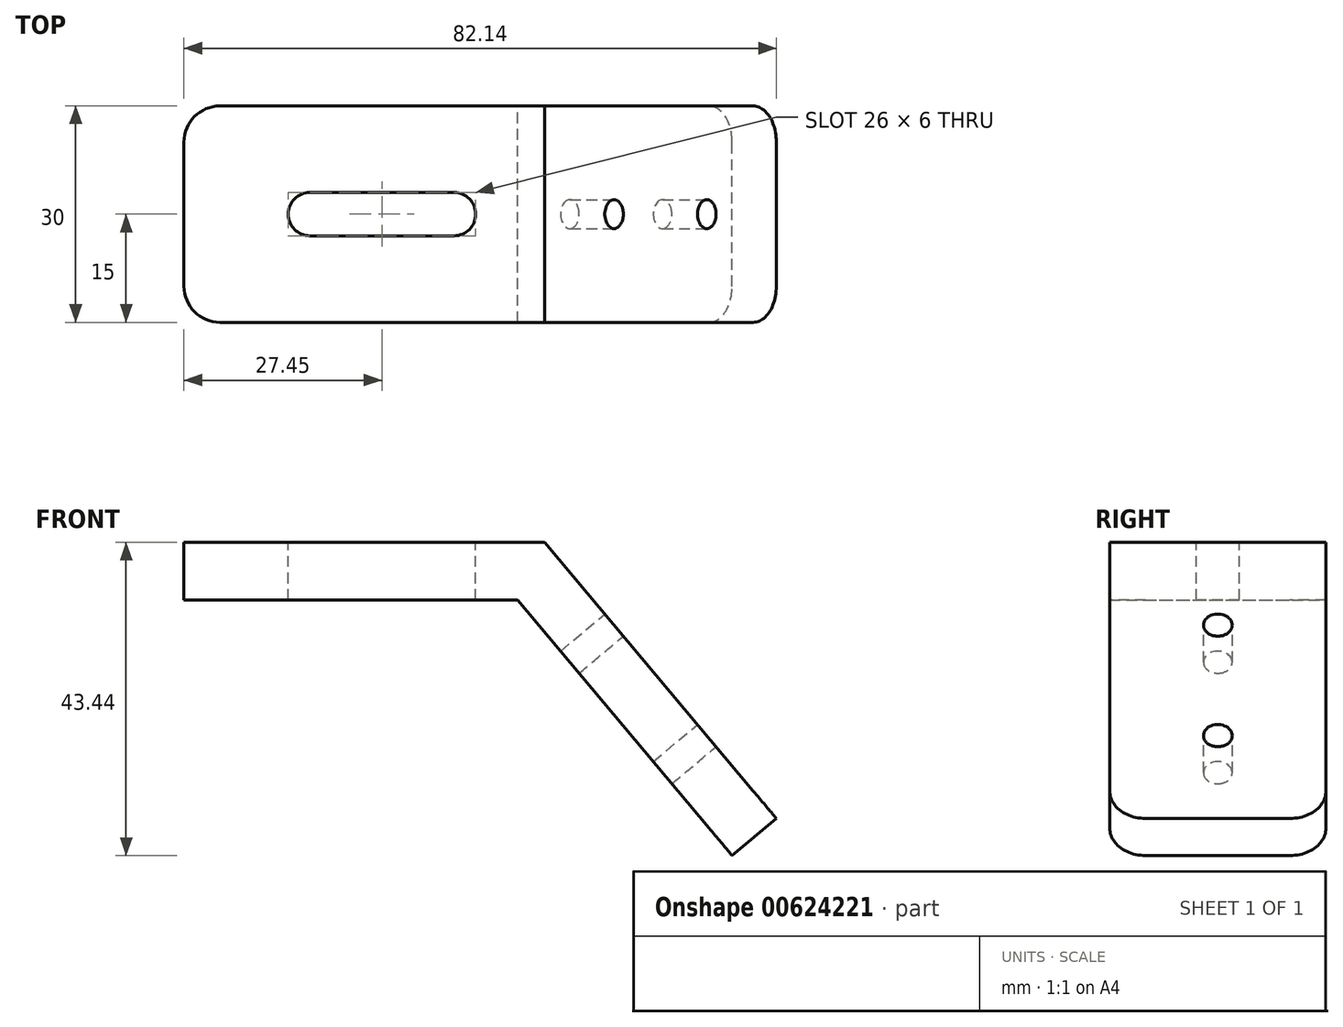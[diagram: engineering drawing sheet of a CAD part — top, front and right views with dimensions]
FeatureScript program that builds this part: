
annotation { "Feature Type Name" : "Feature", "Feature Type Description" : "" }
export const myFeature = defineFeature(function(context is Context, id is Id, definition is map)
    precondition{}
    {
        {
            var Q0;
            Q0=qCreatedBy(makeId("Front.planeOp"),FACE);
            var sketch = newSketch(context, id + "F0", { "sketchPlane" : qUnion([Q0])});
            skLineSegment(sketch, "E0", {"start": v(0, 0) * mm, "end": v(50, 0) * mm});
            skLineSegment(sketch, "E1", {"start": v(50, 0) * mm, "end": v(82.14, -38.3) * mm});
            skLineSegment(sketch, "E2.0", {"start": v(46.27, -8) * mm, "end": v(76.01, -43.44) * mm});
            skLineSegment(sketch, "E2.1", {"start": v(0, -8) * mm, "end": v(46.27, -8) * mm});
            skLineSegment(sketch, "E3", {"start": v(0, 0) * mm, "end": v(0, -8) * mm});
            skLineSegment(sketch, "E4", {"start": v(82.14, -38.3) * mm, "end": v(76.01, -43.44) * mm});
            skSolve(sketch);
        }
        {
            var Q0;
            Q0=makeQuery(id+"F0.imprint","IMPRINT",FACE,{"disambiguationData":[TD([[makeQuery(id+"F0.imprint","IMPRINT",EDGE,{"derivedFrom":sQuery(id+"F0.wireOp",EDGE,"E0")}),-1.0]])]});
            extrude(context, id + "F1", {"entities" : qUnion([Q0]), "endBound" : BoundingType.SYMMETRIC, "depth" : 30 * mm, "offsetDistance" : 25 * mm});
        }
        {
            var Q0;
            Q0=makeQuery(id+"F1.opExtrude","SWEPT_FACE",FACE,{"disambiguationData":[OSD([sQuery(id+"F0.wireOp",EDGE,"E0")])]});
            var sketch = newSketch(context, id + "F2", { "sketchPlane" : qUnion([Q0])});
            skLineSegment(sketch, "E5", {"start": v(17.45, 0) * mm, "end": v(37.45, 0) * mm});
            skArc(sketch, "E6.0.startCap", {"start": v(17.45, -3) * mm, "mid": v(14.45, 0) * mm, "end": v(17.45, 3) * mm});
            skArc(sketch, "E6.0.endCap", {"start": v(37.45, 3) * mm, "mid": v(40.45, 0) * mm, "end": v(37.45, -3) * mm});
            skLineSegment(sketch, "E6.0.left", {"start": v(17.45, 3) * mm, "end": v(37.45, 3) * mm});
            skLineSegment(sketch, "E6.0.right", {"start": v(17.45, -3) * mm, "end": v(37.45, -3) * mm});
            skSolve(sketch);
        }
        {
            var Q0;
            Q0 = qSketchRegion(id + "F2", true);
            extrude(context, id + "F3", {"entities" : qUnion([Q0]), "operationType" : NewBodyOperationType.REMOVE, "endBound" : BoundingType.THROUGH_ALL, "oppositeDirection" : true, "depth" : 25 * mm, "offsetDistance" : 25 * mm});
        }
        {
            var Q0;
            Q0=makeQuery(id+"F1.opExtrude","SWEPT_FACE",FACE,{"disambiguationData":[OSD([sQuery(id+"F0.wireOp",EDGE,"E1")])]});
            var sketch = newSketch(context, id + "F4", { "sketchPlane" : qUnion([Q0])});
            skPoint(sketch, "E7", {"position": v(0, -47.14) * mm});
            skPoint(sketch, "E8", {"position": v(0, -67.14) * mm});
            skSolve(sketch);
        }
        {
            var Q0;
            Q0=sQuery(id+"F4.wireOp",VERTEX,"E7");
            var Q1;
            Q1=sQuery(id+"F4.wireOp",VERTEX,"E8");
            var Q2;
            Q2=makeQuery(id+"F1.opExtrude","SWEPT_BODY",BODY,{"disambiguationData":[OSD([sQuery(id+"F0.wireOp",EDGE,"E0"),sQuery(id+"F0.wireOp",EDGE,"E1"),sQuery(id+"F0.wireOp",EDGE,"E2.0"),sQuery(id+"F0.wireOp",EDGE,"E2.1"),sQuery(id+"F0.wireOp",EDGE,"E3"),sQuery(id+"F0.wireOp",EDGE,"E4")])]});
            hole(context, id + "F5", {"style" : HoleStyle.SIMPLE, "endStyle" : HoleEndStyle.THROUGH, "holeDiameter" : 4 * mm, "majorDiameter" : 5 * mm, "isTappedThrough" : true, "tappedDepth" : 12 * mm, "tapClearance" : 3, "locations" : qUnion([Q0, Q1]), "scope" : qUnion([Q2])});
        }
        {
            var Q0;
            Q0=makeQuery(id+"F1.opExtrude","CAP_EDGE",EDGE,{"disambiguationData":[OSD([sQuery(id+"F0.wireOp",EDGE,"E4")])],"isStart":false});
            var Q1;
            Q1=makeQuery(id+"F1.opExtrude","CAP_EDGE",EDGE,{"disambiguationData":[OSD([sQuery(id+"F0.wireOp",EDGE,"E4")])],"isStart":true});
            var Q2;
            Q2=makeQuery(id+"F1.opExtrude","CAP_EDGE",EDGE,{"disambiguationData":[OSD([sQuery(id+"F0.wireOp",EDGE,"E3")])],"isStart":true});
            var Q3;
            Q3=makeQuery(id+"F1.opExtrude","CAP_EDGE",EDGE,{"disambiguationData":[OSD([sQuery(id+"F0.wireOp",EDGE,"E3")])],"isStart":false});
            fillet(context, id + "F6", {"entities" : qUnion([Q0, Q1, Q2, Q3]), "radius" : 5 * mm, "tangentPropagation" : true, "allowEdgeOverflow" : false});
        }
    });
